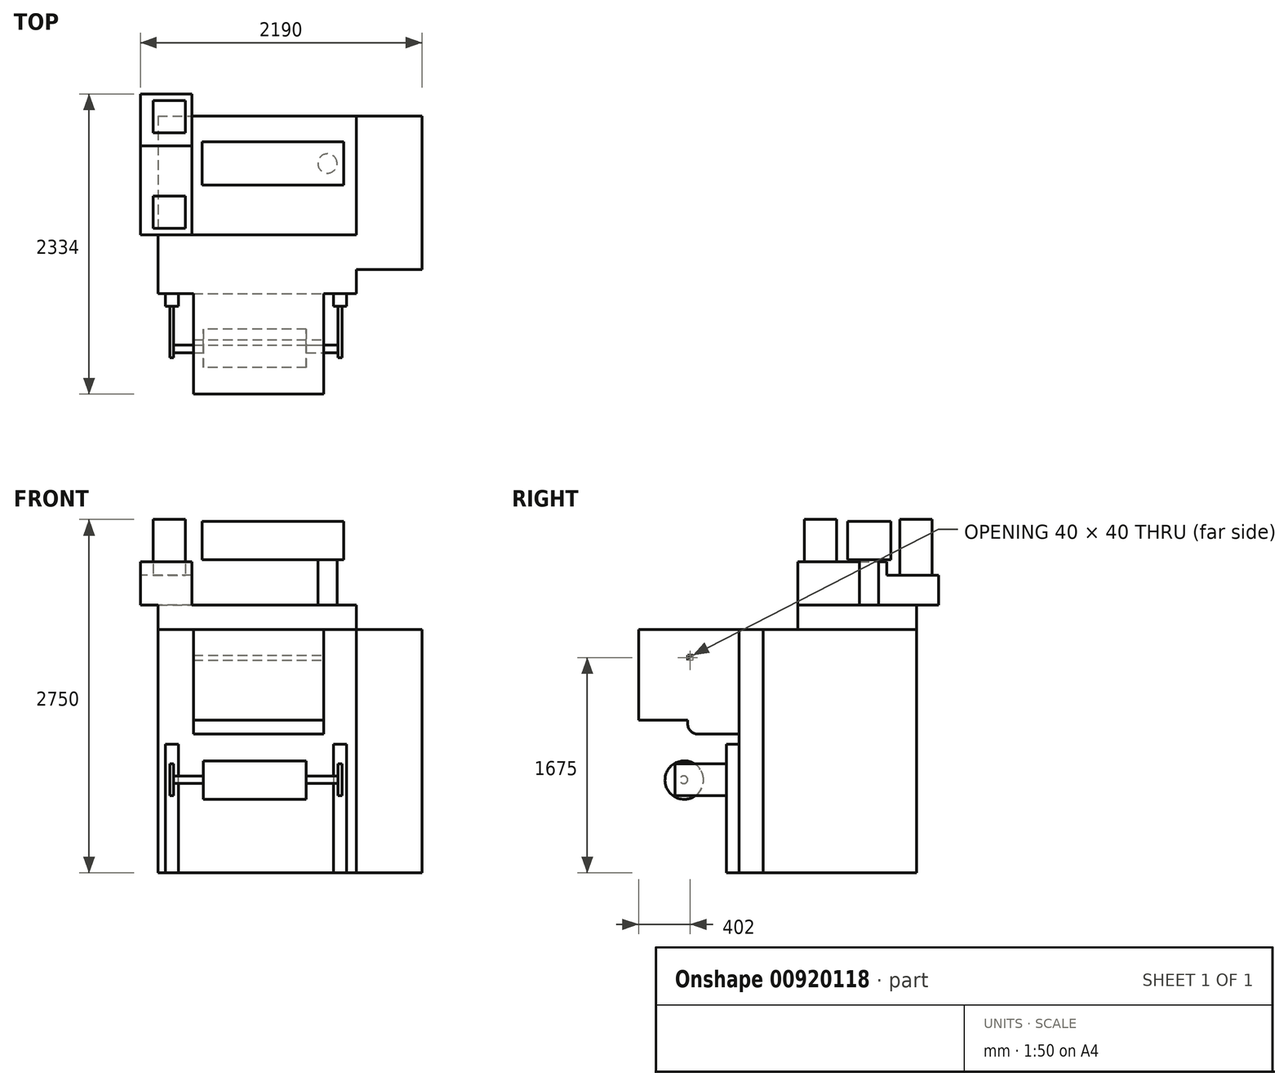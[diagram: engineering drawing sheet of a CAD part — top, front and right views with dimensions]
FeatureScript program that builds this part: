
annotation { "Feature Type Name" : "Feature", "Feature Type Description" : "" }
export const myFeature = defineFeature(function(context is Context, id is Id, definition is map)
    precondition{}
    {
        {
            var Q0;
            Q0=qCreatedBy(makeId("Right.planeOp"),FACE);
            var sketch = newSketch(context, id + "F0", { "sketchPlane" : qUnion([Q0])});
            skLineSegment(sketch, "E0.bottom", {"start": v(597.5, -947.5) * mm, "end": v(-597.5, -947.5) * mm});
            skLineSegment(sketch, "E0.top", {"start": v(597.5, 947.5) * mm, "end": v(-597.5, 947.5) * mm});
            skLineSegment(sketch, "E0.left", {"start": v(597.5, -947.5) * mm, "end": v(597.5, 947.5) * mm});
            skLineSegment(sketch, "E0.right", {"start": v(-597.5, -947.5) * mm, "end": v(-597.5, 947.5) * mm});
            skPoint(sketch, "E0.middle", {"position": v(0, 0) * mm});
            skLineSegment(sketch, "E1", {"start": v(0, 947.5) * mm, "end": v(0, -947.5) * mm});
            skSolve(sketch);
        }
        {
            var Q0;
            Q0 = qSketchRegion(id + "F0", true);
            extrude(context, id + "F1", {"entities" : qUnion([Q0]), "oppositeDirection" : true, "depth" : 510 * mm, "offsetDistance" : 25 * mm});
        }
        {
            var Q0;
            Q0=makeQuery(id+"F1.opExtrude","CAP_FACE",FACE,{"disambiguationData":[OSD([sQuery(id+"F0.wireOp",EDGE,"E0.bottom"),sQuery(id+"F0.wireOp",EDGE,"E0.top"),sQuery(id+"F0.wireOp",EDGE,"E0.left"),sQuery(id+"F0.wireOp",EDGE,"E0.right")])],"isStart":false});
            var sketch = newSketch(context, id + "F2", { "sketchPlane" : qUnion([Q0])});
            skLineSegment(sketch, "E2.bottom", {"start": v(-597.5, 947.5) * mm, "end": v(784.5, 947.5) * mm});
            skLineSegment(sketch, "E2.top", {"start": v(-597.5, -947.5) * mm, "end": v(784.5, -947.5) * mm});
            skLineSegment(sketch, "E2.left", {"start": v(-597.5, 947.5) * mm, "end": v(-597.5, -947.5) * mm});
            skLineSegment(sketch, "E2.right", {"start": v(784.5, 947.5) * mm, "end": v(784.5, -947.5) * mm});
            skSolve(sketch);
        }
        {
            var Q0;
            Q0 = qSketchRegion(id + "F2", true);
            extrude(context, id + "F3", {"entities" : qUnion([Q0]), "operationType" : NewBodyOperationType.ADD, "depth" : 1545 * mm, "offsetDistance" : 25 * mm});
        }
        {
            var Q0;
            Q0=makeQuery(id+"F3.opExtrude","SWEPT_FACE",FACE,{"disambiguationData":[OSD([sQuery(id+"F2.wireOp",EDGE,"E2.right")])]});
            var sketch = newSketch(context, id + "F4", { "sketchPlane" : qUnion([Q0])});
            skLineSegment(sketch, "E3.bottom", {"start": v(-1778, 747.5) * mm, "end": v(-763, 747.5) * mm});
            skLineSegment(sketch, "E3.top", {"start": v(-1778, 132.5) * mm, "end": v(-763, 132.5) * mm});
            skLineSegment(sketch, "E3.left", {"start": v(-1778, 747.5) * mm, "end": v(-1778, 132.5) * mm});
            skLineSegment(sketch, "E3.right", {"start": v(-763, 747.5) * mm, "end": v(-763, 132.5) * mm});
            skSolve(sketch);
        }
        {
            var Q0;
            Q0 = qSketchRegion(id + "F4", true);
            extrude(context, id + "F5", {"entities" : qUnion([Q0]), "operationType" : NewBodyOperationType.ADD, "depth" : 400 * mm, "offsetDistance" : 25 * mm});
        }
        {
            var Q0;
            Q0=makeQuery(id+"F5.opExtrude","CAP_EDGE",EDGE,{"disambiguationData":[OSD([sQuery(id+"F4.wireOp",EDGE,"E3.bottom")])],"isStart":false});
            fillet(context, id + "F6", {"entities" : qUnion([Q0]), "radius" : 40 * mm, "tangentPropagation" : true, "allowEdgeOverflow" : false});
        }
        {
            var Q0;
            Q0=makeQuery(id+"F5.opExtrude","CAP_EDGE",EDGE,{"disambiguationData":[OSD([sQuery(id+"F4.wireOp",EDGE,"E3.top")])],"isStart":false});
            fillet(context, id + "F7", {"entities" : qUnion([Q0]), "radius" : 80 * mm, "tangentPropagation" : true, "allowEdgeOverflow" : false});
        }
        {
            var Q0;
            Q0=makeQuery(id+"F5.opExtrude","SWEPT_FACE",FACE,{"disambiguationData":[OSD([sQuery(id+"F4.wireOp",EDGE,"E3.right")])]});
            var sketch = newSketch(context, id + "F8", { "sketchPlane" : qUnion([Q0])});
            skLineSegment(sketch, "E4", {"start": v(-784.5, 747.5) * mm, "end": v(-784.5, 947.5) * mm});
            skLineSegment(sketch, "E5", {"start": v(-784.5, 947.5) * mm, "end": v(-1566.5, 947.5) * mm});
            skLineSegment(sketch, "E6", {"start": v(-1566.5, 947.5) * mm, "end": v(-1566.5, 242.5) * mm});
            skLineSegment(sketch, "E7", {"start": v(-1566.5, 242.5) * mm, "end": v(-1184.5, 242.5) * mm});
            skPoint(sketch, "E8.endSnap0", {"position": v(-1172.78, 735.78) * mm});
            skLineSegment(sketch, "E9", {"start": v(-784.5, 747.5) * mm, "end": v(-1184.5, 747.5) * mm});
            skLineSegment(sketch, "E10", {"start": v(-1184.5, 747.5) * mm, "end": v(-1184.5, 242.5) * mm});
            skSolve(sketch);
        }
        {
            var Q0;
            Q0 = qSketchRegion(id + "F8", true);
            extrude(context, id + "F9", {"entities" : qUnion([Q0]), "operationType" : NewBodyOperationType.ADD, "oppositeDirection" : true, "depth" : 1015 * mm, "offsetDistance" : 25 * mm});
        }
        {
            var Q0;
            Q0=makeQuery(id+"F9.boolean.opBoolean","MERGE",FACE,{"derivedFrom":[makeQuery(id+"F3.boolean.opBoolean","MERGE",FACE,{"derivedFrom":[makeQuery(id+"F1.opExtrude","SWEPT_FACE",FACE,{"disambiguationData":[OSD([sQuery(id+"F0.wireOp",EDGE,"E0.top")])]}),makeQuery(id+"F3.opExtrude","SWEPT_FACE",FACE,{"disambiguationData":[OSD([sQuery(id+"F2.wireOp",EDGE,"E2.bottom")])]})]}),makeQuery(id+"F9.opExtrude","SWEPT_FACE",FACE,{"disambiguationData":[OSD([sQuery(id+"F8.wireOp",EDGE,"E5")])]})]});
            var sketch = newSketch(context, id + "F10", { "sketchPlane" : qUnion([Q0])});
            skLineSegment(sketch, "E11.bottom", {"start": v(-510, 597.5) * mm, "end": v(-2055, 597.5) * mm});
            skLineSegment(sketch, "E11.top", {"start": v(-510, -327.5) * mm, "end": v(-2055, -327.5) * mm});
            skLineSegment(sketch, "E11.left", {"start": v(-510, 597.5) * mm, "end": v(-510, -327.5) * mm});
            skLineSegment(sketch, "E11.right", {"start": v(-2055, 597.5) * mm, "end": v(-2055, -327.5) * mm});
            skSolve(sketch);
        }
        {
            var Q0;
            Q0 = qSketchRegion(id + "F10", true);
            extrude(context, id + "F11", {"entities" : qUnion([Q0]), "operationType" : NewBodyOperationType.ADD, "depth" : 190 * mm, "offsetDistance" : 25 * mm});
        }
        {
            var Q0;
            Q0=makeQuery(id+"F11.opExtrude","CAP_FACE",FACE,{"disambiguationData":[OSD([sQuery(id+"F10.wireOp",EDGE,"E11.bottom"),sQuery(id+"F10.wireOp",EDGE,"E11.top"),sQuery(id+"F10.wireOp",EDGE,"E11.left"),sQuery(id+"F10.wireOp",EDGE,"E11.right")])],"isStart":false});
            var sketch = newSketch(context, id + "F12", { "sketchPlane" : qUnion([Q0])});
            skCircle(sketch, "E12", {"center": v(-735, 227.5) * mm, "radius": 75 * mm});
            skSolve(sketch);
        }
        {
            var Q0;
            Q0 = qSketchRegion(id + "F12", true);
            extrude(context, id + "F13", {"entities" : qUnion([Q0]), "operationType" : NewBodyOperationType.ADD, "depth" : 350 * mm, "offsetDistance" : 25 * mm});
        }
        {
            var Q0;
            Q0=makeQuery(id+"F13.opExtrude","CAP_FACE",FACE,{"disambiguationData":[OSD([sQuery(id+"F12.wireOp",EDGE,"E12")])],"isStart":false});
            var sketch = newSketch(context, id + "F14", { "sketchPlane" : qUnion([Q0])});
            skLineSegment(sketch, "E13.bottom", {"start": v(-610, 395) * mm, "end": v(-1710, 395) * mm});
            skLineSegment(sketch, "E13.top", {"start": v(-610, 60) * mm, "end": v(-1710, 60) * mm});
            skLineSegment(sketch, "E13.left", {"start": v(-610, 395) * mm, "end": v(-610, 60) * mm});
            skLineSegment(sketch, "E13.right", {"start": v(-1710, 395) * mm, "end": v(-1710, 60) * mm});
            skSolve(sketch);
        }
        {
            var Q0;
            Q0 = qSketchRegion(id + "F14", true);
            extrude(context, id + "F15", {"entities" : qUnion([Q0]), "operationType" : NewBodyOperationType.ADD, "depth" : 300 * mm, "offsetDistance" : 25 * mm});
        }
        {
            var Q0;
            Q0=makeQuery(id+"F11.opExtrude","CAP_FACE",FACE,{"disambiguationData":[OSD([sQuery(id+"F10.wireOp",EDGE,"E11.bottom"),sQuery(id+"F10.wireOp",EDGE,"E11.top"),sQuery(id+"F10.wireOp",EDGE,"E11.left"),sQuery(id+"F10.wireOp",EDGE,"E11.right")])],"isStart":false});
            var sketch = newSketch(context, id + "F16", { "sketchPlane" : qUnion([Q0])});
            skLineSegment(sketch, "E14.bottom", {"start": v(-1790, -327.5) * mm, "end": v(-2190, -327.5) * mm});
            skLineSegment(sketch, "E14.top", {"start": v(-1790, 767.5) * mm, "end": v(-2190, 767.5) * mm});
            skLineSegment(sketch, "E14.left", {"start": v(-1790, -327.5) * mm, "end": v(-1790, 767.5) * mm});
            skLineSegment(sketch, "E14.right", {"start": v(-2190, -327.5) * mm, "end": v(-2190, 767.5) * mm});
            skSolve(sketch);
        }
        {
            var Q0;
            Q0 = qSketchRegion(id + "F16", true);
            extrude(context, id + "F17", {"entities" : qUnion([Q0]), "operationType" : NewBodyOperationType.ADD, "depth" : 335 * mm, "offsetDistance" : 25 * mm});
        }
        {
            var Q0;
            Q0=makeQuery(id+"F17.opExtrude","SWEPT_FACE",FACE,{"disambiguationData":[OSD([sQuery(id+"F16.wireOp",EDGE,"E14.right")])]});
            var sketch = newSketch(context, id + "F18", { "sketchPlane" : qUnion([Q0])});
            skLineSegment(sketch, "E15.bottom", {"start": v(-767.5, 1472.5) * mm, "end": v(-365.5, 1472.5) * mm});
            skLineSegment(sketch, "E15.top", {"start": v(-767.5, 1367.5) * mm, "end": v(-365.5, 1367.5) * mm});
            skLineSegment(sketch, "E15.left", {"start": v(-767.5, 1472.5) * mm, "end": v(-767.5, 1367.5) * mm});
            skLineSegment(sketch, "E15.right", {"start": v(-365.5, 1472.5) * mm, "end": v(-365.5, 1367.5) * mm});
            skSolve(sketch);
        }
        {
            var Q0;
            Q0 = qSketchRegion(id + "F18", true);
            extrude(context, id + "F19", {"entities" : qUnion([Q0]), "operationType" : NewBodyOperationType.REMOVE, "endBound" : BoundingType.UP_TO_NEXT, "oppositeDirection" : true, "depth" : 25 * mm, "offsetDistance" : 25 * mm});
        }
        {
            var Q0;
            Q0=makeQuery(id+"F19.boolean.opBoolean","COPY",FACE,{"derivedFrom":makeQuery(id+"F19.opExtrude","SWEPT_FACE",FACE,{"disambiguationData":[OSD([sQuery(id+"F18.wireOp",EDGE,"E15.top")])]})});
            var sketch = newSketch(context, id + "F20", { "sketchPlane" : qUnion([Q0])});
            skLineSegment(sketch, "E16.bottom", {"start": v(-2090, 717.5) * mm, "end": v(-1840, 717.5) * mm});
            skLineSegment(sketch, "E16.top", {"start": v(-2090, 465.5) * mm, "end": v(-1840, 465.5) * mm});
            skLineSegment(sketch, "E16.left", {"start": v(-2090, 717.5) * mm, "end": v(-2090, 465.5) * mm});
            skLineSegment(sketch, "E16.right", {"start": v(-1840, 717.5) * mm, "end": v(-1840, 465.5) * mm});
            skSolve(sketch);
        }
        {
            var Q0;
            Q0 = qSketchRegion(id + "F20", true);
            extrude(context, id + "F21", {"entities" : qUnion([Q0]), "operationType" : NewBodyOperationType.ADD, "depth" : 435 * mm, "offsetDistance" : 25 * mm});
        }
        {
            var Q0;
            Q0=makeQuery(id+"F17.opExtrude","CAP_FACE",FACE,{"disambiguationData":[OSD([sQuery(id+"F16.wireOp",EDGE,"E14.bottom"),sQuery(id+"F16.wireOp",EDGE,"E14.top"),sQuery(id+"F16.wireOp",EDGE,"E14.left"),sQuery(id+"F16.wireOp",EDGE,"E14.right")])],"isStart":false});
            var sketch = newSketch(context, id + "F22", { "sketchPlane" : qUnion([Q0])});
            skLineSegment(sketch, "E17.bottom", {"start": v(-2090, -25.5) * mm, "end": v(-1840, -25.5) * mm});
            skLineSegment(sketch, "E17.top", {"start": v(-2090, -277.5) * mm, "end": v(-1840, -277.5) * mm});
            skLineSegment(sketch, "E17.left", {"start": v(-2090, -25.5) * mm, "end": v(-2090, -277.5) * mm});
            skLineSegment(sketch, "E17.right", {"start": v(-1840, -25.5) * mm, "end": v(-1840, -277.5) * mm});
            skSolve(sketch);
        }
        {
            var Q0;
            Q0 = qSketchRegion(id + "F22", true);
            extrude(context, id + "F23", {"entities" : qUnion([Q0]), "operationType" : NewBodyOperationType.ADD, "depth" : 330 * mm, "offsetDistance" : 25 * mm});
        }
        {
            var Q0;
            Q0=makeQuery(id+"F3.opExtrude","SWEPT_FACE",FACE,{"disambiguationData":[OSD([sQuery(id+"F2.wireOp",EDGE,"E2.right")])]});
            var sketch = newSketch(context, id + "F24", { "sketchPlane" : qUnion([Q0])});
            skLineSegment(sketch, "E18.bottom", {"start": v(-587.54, 52.5) * mm, "end": v(-687.54, 52.5) * mm});
            skLineSegment(sketch, "E18.top", {"start": v(-587.54, -947.5) * mm, "end": v(-687.54, -947.5) * mm});
            skLineSegment(sketch, "E18.left", {"start": v(-587.54, 52.5) * mm, "end": v(-587.54, -947.5) * mm});
            skLineSegment(sketch, "E18.right", {"start": v(-687.54, 52.5) * mm, "end": v(-687.54, -947.5) * mm});
            skSolve(sketch);
        }
        {
            var Q0;
            Q0 = qSketchRegion(id + "F24", true);
            extrude(context, id + "F25", {"entities" : qUnion([Q0]), "operationType" : NewBodyOperationType.ADD, "depth" : 100 * mm, "offsetDistance" : 25 * mm});
        }
        {
            var Q0;
            Q0=makeQuery(id+"F3.opExtrude","SWEPT_FACE",FACE,{"disambiguationData":[OSD([sQuery(id+"F2.wireOp",EDGE,"E2.right")])]});
            var sketch = newSketch(context, id + "F26", { "sketchPlane" : qUnion([Q0])});
            skPoint(sketch, "E19.oppositeSnap0", {"position": v(-637.54, 52.5) * mm});
            skLineSegment(sketch, "E19.bottom", {"start": v(-1994.86, -947.5) * mm, "end": v(-1894.86, -947.5) * mm});
            skLineSegment(sketch, "E19.top", {"start": v(-1994.86, 52.5) * mm, "end": v(-1894.86, 52.5) * mm});
            skLineSegment(sketch, "E19.left", {"start": v(-1994.86, -947.5) * mm, "end": v(-1994.86, 52.5) * mm});
            skLineSegment(sketch, "E19.right", {"start": v(-1894.86, -947.5) * mm, "end": v(-1894.86, 52.5) * mm});
            skSolve(sketch);
        }
        {
            var Q0;
            Q0 = qSketchRegion(id + "F26", true);
            extrude(context, id + "F27", {"entities" : qUnion([Q0]), "operationType" : NewBodyOperationType.ADD, "depth" : 100 * mm, "offsetDistance" : 25 * mm});
        }
        {
            var Q0;
            Q0=makeQuery(id+"F25.opExtrude","CAP_FACE",FACE,{"disambiguationData":[OSD([sQuery(id+"F24.wireOp",EDGE,"E18.bottom"),sQuery(id+"F24.wireOp",EDGE,"E18.top"),sQuery(id+"F24.wireOp",EDGE,"E18.left"),sQuery(id+"F24.wireOp",EDGE,"E18.right")])],"isStart":false});
            var sketch = newSketch(context, id + "F28", { "sketchPlane" : qUnion([Q0])});
            skLineSegment(sketch, "E20.bottom", {"start": v(-652.36, -97.5) * mm, "end": v(-622.36, -97.5) * mm});
            skLineSegment(sketch, "E20.top", {"start": v(-652.36, -347.5) * mm, "end": v(-622.36, -347.5) * mm});
            skLineSegment(sketch, "E20.left", {"start": v(-652.36, -97.5) * mm, "end": v(-652.36, -347.5) * mm});
            skLineSegment(sketch, "E20.right", {"start": v(-622.36, -97.5) * mm, "end": v(-622.36, -347.5) * mm});
            skLineSegment(sketch, "E21.1.0.0", {"start": v(-1932.36, -97.5) * mm, "end": v(-1932.36, -347.5) * mm});
            skLineSegment(sketch, "E21.1.0.1", {"start": v(-1962.36, -97.5) * mm, "end": v(-1932.36, -97.5) * mm});
            skLineSegment(sketch, "E21.1.0.2", {"start": v(-1962.36, -97.5) * mm, "end": v(-1962.36, -347.5) * mm});
            skLineSegment(sketch, "E21.1.0.3", {"start": v(-1962.36, -347.5) * mm, "end": v(-1932.36, -347.5) * mm});
            skLineSegment(sketch, "E21.direction1", {"start": v(-622.36, -347.5) * mm, "end": v(-1932.36, -347.5) * mm, "construction": true});
            skSolve(sketch);
        }
        {
            var Q0;
            Q0=makeQuery(id+"F28.imprint","IMPRINT",FACE,{"disambiguationData":[TD([[makeQuery(id+"F28.imprint","IMPRINT",EDGE,{"derivedFrom":sQuery(id+"F28.wireOp",EDGE,"E20.bottom")}),-1.0]])]});
            var Q1;
            Q1=makeQuery(id+"F28.imprint","IMPRINT",FACE,{"disambiguationData":[TD([[makeQuery(id+"F28.imprint","IMPRINT",EDGE,{"derivedFrom":sQuery(id+"F28.wireOp",EDGE,"E21.1.0.0")}),-1.0]])]});
            extrude(context, id + "F29", {"entities" : qUnion([Q0, Q1]), "operationType" : NewBodyOperationType.ADD, "depth" : 400 * mm, "offsetDistance" : 25 * mm});
        }
        {
            var Q0;
            Q0=makeQuery(id+"F29.opExtrude","SWEPT_FACE",FACE,{"disambiguationData":[OSD([sQuery(id+"F28.wireOp",EDGE,"E20.right")])]});
            var sketch = newSketch(context, id + "F30", { "sketchPlane" : qUnion([Q0])});
            skCircle(sketch, "E22", {"center": v(-1214.5, -222.5) * mm, "radius": 30 * mm});
            skSolve(sketch);
        }
        {
            var Q0;
            Q0 = qSketchRegion(id + "F30", true);
            var Q1;
            Q1=makeQuery(id+"F29.opExtrude","SWEPT_FACE",FACE,{"disambiguationData":[OSD([sQuery(id+"F28.wireOp",EDGE,"E21.1.0.0")])]});
            extrude(context, id + "F31", {"entities" : qUnion([Q0]), "operationType" : NewBodyOperationType.ADD, "endBound" : BoundingType.UP_TO_SURFACE, "oppositeDirection" : true, "depth" : 25 * mm, "endBoundEntityFace" : qUnion([Q1]), "offsetDistance" : 25 * mm});
        }
        {
            var Q0;
            Q0=qCreatedBy(makeId("Right.planeOp"),FACE);
            cPlane(context, id + "F32", {"entities" : qUnion([Q0]), "cplaneType" : CPlaneType.OFFSET, "offset" : 1300 * mm, "oppositeDirection" : true, "width" : 150 * mm, "height" : 150 * mm});
        }
        {
            var Q0;
            Q0=qCreatedBy(id+"F32.planeOp",FACE);
            var sketch = newSketch(context, id + "F33", { "sketchPlane" : qUnion([Q0])});
            skCircle(sketch, "E23", {"center": v(-1211.05, -225) * mm, "radius": 150 * mm});
            skSolve(sketch);
        }
        {
            var Q0;
            Q0 = qSketchRegion(id + "F33", true);
            extrude(context, id + "F34", {"entities" : qUnion([Q0]), "operationType" : NewBodyOperationType.ADD, "endBound" : BoundingType.SYMMETRIC, "depth" : 800 * mm, "offsetDistance" : 25 * mm});
        }
    });
